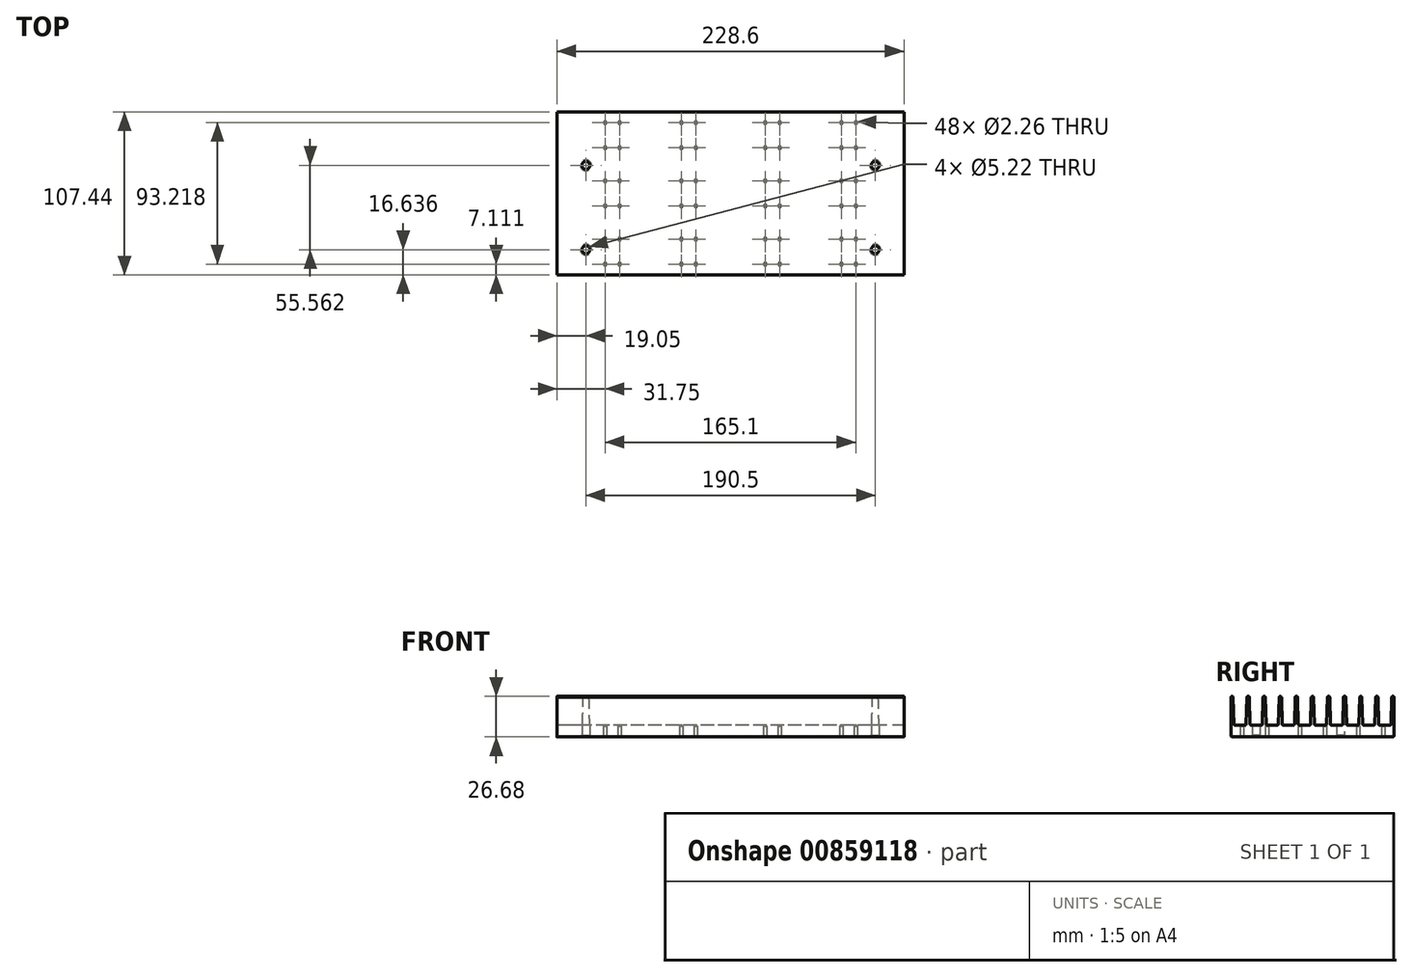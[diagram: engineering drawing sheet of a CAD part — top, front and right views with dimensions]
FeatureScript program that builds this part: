
annotation { "Feature Type Name" : "Feature", "Feature Type Description" : "" }
export const myFeature = defineFeature(function(context is Context, id is Id, definition is map)
    precondition{}
    {
        {
            var Q0;
            Q0=qCreatedBy(makeId("Right.planeOp"),FACE);
            var sketch = newSketch(context, id + "F0", { "sketchPlane" : qUnion([Q0])});
            skLineSegment(sketch, "E0", {"start": v(50.94, -5.71) * mm, "end": v(44.38, -5.71) * mm});
            skArc(sketch, "E1", {"start": v(43.62, -4.97) * mm, "mid": v(43.85, -5.5) * mm, "end": v(44.38, -5.71) * mm});
            skLineSegment(sketch, "E2", {"start": v(43.62, -4.97) * mm, "end": v(43.13, 12.59) * mm});
            skArc(sketch, "E3", {"start": v(43.13, 12.59) * mm, "mid": v(42.37, 13.33) * mm, "end": v(41.6, 12.59) * mm});
            skLineSegment(sketch, "E4", {"start": v(41.6, 12.59) * mm, "end": v(41.11, -4.97) * mm});
            skArc(sketch, "E5", {"start": v(40.35, -5.71) * mm, "mid": v(40.88, -5.5) * mm, "end": v(41.11, -4.97) * mm});
            skLineSegment(sketch, "E6", {"start": v(40.35, -5.71) * mm, "end": v(33.8, -5.71) * mm});
            skArc(sketch, "E7", {"start": v(33.03, -4.97) * mm, "mid": v(33.26, -5.5) * mm, "end": v(33.8, -5.71) * mm});
            skLineSegment(sketch, "E8", {"start": v(33.03, -4.97) * mm, "end": v(32.54, 12.59) * mm});
            skArc(sketch, "E9", {"start": v(32.54, 12.59) * mm, "mid": v(31.78, 13.33) * mm, "end": v(31.01, 12.59) * mm});
            skLineSegment(sketch, "E10", {"start": v(31.01, 12.59) * mm, "end": v(30.52, -4.97) * mm});
            skArc(sketch, "E11", {"start": v(29.76, -5.71) * mm, "mid": v(30.3, -5.5) * mm, "end": v(30.52, -4.97) * mm});
            skLineSegment(sketch, "E12", {"start": v(29.76, -5.71) * mm, "end": v(23.2, -5.71) * mm});
            skArc(sketch, "E13", {"start": v(22.44, -4.97) * mm, "mid": v(22.67, -5.5) * mm, "end": v(23.2, -5.71) * mm});
            skLineSegment(sketch, "E14", {"start": v(22.44, -4.97) * mm, "end": v(21.95, 12.59) * mm});
            skArc(sketch, "E15", {"start": v(21.95, 12.59) * mm, "mid": v(21.18, 13.33) * mm, "end": v(20.42, 12.59) * mm});
            skLineSegment(sketch, "E16", {"start": v(20.42, 12.59) * mm, "end": v(19.93, -4.97) * mm});
            skArc(sketch, "E17", {"start": v(19.17, -5.71) * mm, "mid": v(19.7, -5.5) * mm, "end": v(19.93, -4.97) * mm});
            skLineSegment(sketch, "E18", {"start": v(19.17, -5.71) * mm, "end": v(12.6, -5.71) * mm});
            skArc(sketch, "E19", {"start": v(11.85, -4.97) * mm, "mid": v(12.08, -5.5) * mm, "end": v(12.6, -5.71) * mm});
            skLineSegment(sketch, "E20", {"start": v(11.85, -4.97) * mm, "end": v(11.35, 12.59) * mm});
            skArc(sketch, "E21", {"start": v(11.35, 12.59) * mm, "mid": v(10.6, 13.33) * mm, "end": v(9.83, 12.59) * mm});
            skLineSegment(sketch, "E22", {"start": v(9.83, 12.59) * mm, "end": v(9.34, -4.97) * mm});
            skArc(sketch, "E23", {"start": v(8.58, -5.71) * mm, "mid": v(9.1, -5.5) * mm, "end": v(9.34, -4.97) * mm});
            skLineSegment(sketch, "E24", {"start": v(8.58, -5.71) * mm, "end": v(2.02, -5.71) * mm});
            skArc(sketch, "E25", {"start": v(1.25, -4.97) * mm, "mid": v(1.48, -5.5) * mm, "end": v(2.02, -5.71) * mm});
            skLineSegment(sketch, "E26", {"start": v(1.25, -4.97) * mm, "end": v(0.76, 12.59) * mm});
            skArc(sketch, "E27", {"start": v(0.76, 12.59) * mm, "mid": v(0, 13.33) * mm, "end": v(-0.76, 12.59) * mm});
            skLineSegment(sketch, "E28", {"start": v(-0.76, 12.59) * mm, "end": v(-1.25, -4.97) * mm});
            skArc(sketch, "E29", {"start": v(-2.02, -5.71) * mm, "mid": v(-1.48, -5.5) * mm, "end": v(-1.25, -4.97) * mm});
            skLineSegment(sketch, "E30", {"start": v(-2.02, -5.71) * mm, "end": v(-8.58, -5.71) * mm});
            skArc(sketch, "E31", {"start": v(-9.34, -4.97) * mm, "mid": v(-9.1, -5.5) * mm, "end": v(-8.58, -5.71) * mm});
            skLineSegment(sketch, "E32", {"start": v(-9.34, -4.97) * mm, "end": v(-9.83, 12.59) * mm});
            skArc(sketch, "E33", {"start": v(-9.83, 12.59) * mm, "mid": v(-10.6, 13.33) * mm, "end": v(-11.35, 12.59) * mm});
            skLineSegment(sketch, "E34", {"start": v(-11.35, 12.59) * mm, "end": v(-11.85, -4.97) * mm});
            skArc(sketch, "E35", {"start": v(-12.6, -5.71) * mm, "mid": v(-12.08, -5.5) * mm, "end": v(-11.85, -4.97) * mm});
            skLineSegment(sketch, "E36", {"start": v(-12.6, -5.71) * mm, "end": v(-19.17, -5.71) * mm});
            skArc(sketch, "E37", {"start": v(-19.93, -4.97) * mm, "mid": v(-19.7, -5.5) * mm, "end": v(-19.17, -5.71) * mm});
            skLineSegment(sketch, "E38", {"start": v(-19.93, -4.97) * mm, "end": v(-20.42, 12.59) * mm});
            skArc(sketch, "E39", {"start": v(-20.42, 12.59) * mm, "mid": v(-21.18, 13.34) * mm, "end": v(-21.95, 12.59) * mm});
            skLineSegment(sketch, "E40", {"start": v(-21.95, 12.59) * mm, "end": v(-22.44, -4.97) * mm});
            skArc(sketch, "E41", {"start": v(-23.2, -5.71) * mm, "mid": v(-22.67, -5.5) * mm, "end": v(-22.44, -4.97) * mm});
            skLineSegment(sketch, "E42", {"start": v(-23.2, -5.71) * mm, "end": v(-29.76, -5.71) * mm});
            skArc(sketch, "E43", {"start": v(-30.52, -4.97) * mm, "mid": v(-30.3, -5.5) * mm, "end": v(-29.76, -5.71) * mm});
            skLineSegment(sketch, "E44", {"start": v(-30.52, -4.97) * mm, "end": v(-31.01, 12.59) * mm});
            skArc(sketch, "E45", {"start": v(-31.01, 12.59) * mm, "mid": v(-31.78, 13.33) * mm, "end": v(-32.54, 12.59) * mm});
            skLineSegment(sketch, "E46", {"start": v(-32.54, 12.59) * mm, "end": v(-33.03, -4.97) * mm});
            skArc(sketch, "E47", {"start": v(-33.8, -5.71) * mm, "mid": v(-33.26, -5.5) * mm, "end": v(-33.03, -4.97) * mm});
            skLineSegment(sketch, "E48", {"start": v(-33.8, -5.71) * mm, "end": v(-40.35, -5.71) * mm});
            skArc(sketch, "E49", {"start": v(-41.11, -4.97) * mm, "mid": v(-40.88, -5.5) * mm, "end": v(-40.35, -5.71) * mm});
            skLineSegment(sketch, "E50", {"start": v(-41.11, -4.97) * mm, "end": v(-41.6, 12.59) * mm});
            skArc(sketch, "E51", {"start": v(-41.6, 12.59) * mm, "mid": v(-42.37, 13.33) * mm, "end": v(-43.13, 12.59) * mm});
            skLineSegment(sketch, "E52", {"start": v(-43.13, 12.59) * mm, "end": v(-43.62, -4.97) * mm});
            skArc(sketch, "E53", {"start": v(-44.38, -5.71) * mm, "mid": v(-43.85, -5.5) * mm, "end": v(-43.62, -4.97) * mm});
            skLineSegment(sketch, "E54", {"start": v(-44.38, -5.71) * mm, "end": v(-50.94, -5.71) * mm});
            skArc(sketch, "E55", {"start": v(-51.7, -4.97) * mm, "mid": v(-51.48, -5.5) * mm, "end": v(-50.94, -5.71) * mm});
            skLineSegment(sketch, "E56", {"start": v(-51.7, -4.97) * mm, "end": v(-52.2, 12.59) * mm});
            skArc(sketch, "E57", {"start": v(-52.2, 12.59) * mm, "mid": v(-52.96, 13.34) * mm, "end": v(-53.72, 12.59) * mm});
            skLineSegment(sketch, "E58", {"start": v(-53.72, 12.59) * mm, "end": v(-53.72, -12.57) * mm});
            skArc(sketch, "E59", {"start": v(-53.72, -12.57) * mm, "mid": v(-53.5, -13.11) * mm, "end": v(-52.96, -13.34) * mm});
            skLineSegment(sketch, "E60", {"start": v(-52.96, -13.33) * mm, "end": v(52.96, -13.33) * mm});
            skArc(sketch, "E61", {"start": v(52.96, -13.34) * mm, "mid": v(53.5, -13.11) * mm, "end": v(53.72, -12.57) * mm});
            skLineSegment(sketch, "E62", {"start": v(53.72, -12.57) * mm, "end": v(53.72, 12.59) * mm});
            skArc(sketch, "E63", {"start": v(53.72, 12.59) * mm, "mid": v(52.96, 13.33) * mm, "end": v(52.2, 12.59) * mm});
            skLineSegment(sketch, "E64", {"start": v(52.2, 12.59) * mm, "end": v(51.7, -4.97) * mm});
            skArc(sketch, "E65", {"start": v(50.94, -5.71) * mm, "mid": v(51.48, -5.5) * mm, "end": v(51.7, -4.97) * mm});
            skSolve(sketch);
        }
        {
            var Q0;
            Q0=qSketchRegion(id+"F0",true);
            extrude(context, id + "F1", {"entities" : qUnion([Q0]), "endBound" : BoundingType.SYMMETRIC, "depth" : 228.6 * mm, "offsetDistance" : 25.4 * mm});
        }
        {
            var Q0;
            Q0=makeQuery(id+"F1.opExtrude","SWEPT_FACE",FACE,{"disambiguationData":[OSD([sQuery(id+"F0.wireOp",EDGE,"E60")])]});
            var sketch = newSketch(context, id + "F2", { "sketchPlane" : qUnion([Q0])});
            skLineSegment(sketch, "E66.0", {"start": v(-114.3, 52.96) * mm, "end": v(-114.3, -52.96) * mm});
            skLineSegment(sketch, "E67.0.2", {"start": v(114.3, -52.96) * mm, "end": v(114.3, 52.96) * mm});
            skPoint(sketch, "E68", {"position": v(-95.25, 37.08) * mm});
            skPoint(sketch, "E69", {"position": v(95.25, 37.08) * mm});
            skPoint(sketch, "E70", {"position": v(14.56, 92.82) * mm});
            skPoint(sketch, "E71", {"position": v(-95.25, -18.48) * mm});
            skPoint(sketch, "E72", {"position": v(95.25, -18.48) * mm});
            skSolve(sketch);
        }
        {
            var Q0;
            Q0=sQuery(id+"F2.wireOp",VERTEX,"E68");
            var Q1;
            Q1=sQuery(id+"F2.wireOp",VERTEX,"E71");
            var Q2;
            Q2=sQuery(id+"F2.wireOp",VERTEX,"E69");
            var Q3;
            Q3=sQuery(id+"F2.wireOp",VERTEX,"E72");
            var Q4;
            Q4=makeQuery(id+"F1.opExtrude","SWEPT_BODY",BODY,{"disambiguationData":[OSD([sQuery(id+"F0.wireOp",EDGE,"E0"),sQuery(id+"F0.wireOp",EDGE,"E1"),sQuery(id+"F0.wireOp",EDGE,"E2"),sQuery(id+"F0.wireOp",EDGE,"E3"),sQuery(id+"F0.wireOp",EDGE,"E4"),sQuery(id+"F0.wireOp",EDGE,"E5"),sQuery(id+"F0.wireOp",EDGE,"E6"),sQuery(id+"F0.wireOp",EDGE,"E7"),sQuery(id+"F0.wireOp",EDGE,"E8"),sQuery(id+"F0.wireOp",EDGE,"E9"),sQuery(id+"F0.wireOp",EDGE,"E10"),sQuery(id+"F0.wireOp",EDGE,"E11"),sQuery(id+"F0.wireOp",EDGE,"E12"),sQuery(id+"F0.wireOp",EDGE,"E13"),sQuery(id+"F0.wireOp",EDGE,"E14"),sQuery(id+"F0.wireOp",EDGE,"E15"),sQuery(id+"F0.wireOp",EDGE,"E16"),sQuery(id+"F0.wireOp",EDGE,"E17"),sQuery(id+"F0.wireOp",EDGE,"E18"),sQuery(id+"F0.wireOp",EDGE,"E19"),sQuery(id+"F0.wireOp",EDGE,"E20"),sQuery(id+"F0.wireOp",EDGE,"E21"),sQuery(id+"F0.wireOp",EDGE,"E22"),sQuery(id+"F0.wireOp",EDGE,"E23"),sQuery(id+"F0.wireOp",EDGE,"E24"),sQuery(id+"F0.wireOp",EDGE,"E25"),sQuery(id+"F0.wireOp",EDGE,"E26"),sQuery(id+"F0.wireOp",EDGE,"E27"),sQuery(id+"F0.wireOp",EDGE,"E28"),sQuery(id+"F0.wireOp",EDGE,"E29"),sQuery(id+"F0.wireOp",EDGE,"E30"),sQuery(id+"F0.wireOp",EDGE,"E31"),sQuery(id+"F0.wireOp",EDGE,"E32"),sQuery(id+"F0.wireOp",EDGE,"E33"),sQuery(id+"F0.wireOp",EDGE,"E34"),sQuery(id+"F0.wireOp",EDGE,"E35"),sQuery(id+"F0.wireOp",EDGE,"E36"),sQuery(id+"F0.wireOp",EDGE,"E37"),sQuery(id+"F0.wireOp",EDGE,"E38"),sQuery(id+"F0.wireOp",EDGE,"E39"),sQuery(id+"F0.wireOp",EDGE,"E40"),sQuery(id+"F0.wireOp",EDGE,"E41"),sQuery(id+"F0.wireOp",EDGE,"E42"),sQuery(id+"F0.wireOp",EDGE,"E43"),sQuery(id+"F0.wireOp",EDGE,"E44"),sQuery(id+"F0.wireOp",EDGE,"E45"),sQuery(id+"F0.wireOp",EDGE,"E46"),sQuery(id+"F0.wireOp",EDGE,"E47"),sQuery(id+"F0.wireOp",EDGE,"E48"),sQuery(id+"F0.wireOp",EDGE,"E49"),sQuery(id+"F0.wireOp",EDGE,"E50"),sQuery(id+"F0.wireOp",EDGE,"E51"),sQuery(id+"F0.wireOp",EDGE,"E52"),sQuery(id+"F0.wireOp",EDGE,"E53"),sQuery(id+"F0.wireOp",EDGE,"E54"),sQuery(id+"F0.wireOp",EDGE,"E55"),sQuery(id+"F0.wireOp",EDGE,"E56"),sQuery(id+"F0.wireOp",EDGE,"E57"),sQuery(id+"F0.wireOp",EDGE,"E58"),sQuery(id+"F0.wireOp",EDGE,"E59"),sQuery(id+"F0.wireOp",EDGE,"E60"),sQuery(id+"F0.wireOp",EDGE,"E61"),sQuery(id+"F0.wireOp",EDGE,"E62"),sQuery(id+"F0.wireOp",EDGE,"E63"),sQuery(id+"F0.wireOp",EDGE,"E64"),sQuery(id+"F0.wireOp",EDGE,"E65")])]});
            hole(context, id + "F3", {"style" : HoleStyle.C_SINK, "endStyle" : HoleEndStyle.THROUGH, "standardTappedOrClearance" : lookupTablePath({ "standard" : "ANSI", "size" : "#5 (0.2)", "type" : "Drilled" }), "standardBlindInLast" : lookupTablePath({ "standard" : "ANSI", "size" : "#5", "type" : "Drilled" }), "holeDiameter" : 5.22 * mm, "cSinkDiameter" : 7.14 * mm, "cSinkAngle" : 82 * degree, "majorDiameter" : 2.84 * mm, "isTappedThrough" : true, "tappedDepth" : 5.2 * mm, "tapClearance" : 3, "locations" : qUnion([Q0, Q1, Q2, Q3]), "scope" : qUnion([Q4])});
        }
        {
            var Q0;
            Q0=makeQuery(id+"F1.opExtrude","SWEPT_FACE",FACE,{"disambiguationData":[OSD([sQuery(id+"F0.wireOp",EDGE,"E60")])]});
            var sketch = newSketch(context, id + "F4", { "sketchPlane" : qUnion([Q0])});
            skPoint(sketch, "E73", {"position": v(-82.55, 46.6) * mm});
            skPoint(sketch, "E74", {"position": v(-73.03, 46.6) * mm});
            skPoint(sketch, "E75", {"position": v(-82.55, 30.1) * mm});
            skPoint(sketch, "E76", {"position": v(-73.03, 30.1) * mm});
            skPoint(sketch, "E77", {"position": v(-32.38, 46.6) * mm});
            skPoint(sketch, "E78", {"position": v(-22.86, 46.6) * mm});
            skPoint(sketch, "E79", {"position": v(-32.38, 30.1) * mm});
            skPoint(sketch, "E80", {"position": v(-22.86, 30.1) * mm});
            skPoint(sketch, "E81.MirrorP", {"position": v(82.55, 46.6) * mm});
            skPoint(sketch, "E82.MirrorP", {"position": v(73.03, 46.6) * mm});
            skPoint(sketch, "E83.MirrorP", {"position": v(82.55, 30.1) * mm});
            skPoint(sketch, "E84.MirrorP", {"position": v(73.03, 30.1) * mm});
            skPoint(sketch, "E85.MirrorP", {"position": v(32.38, 46.6) * mm});
            skPoint(sketch, "E86.MirrorP", {"position": v(22.86, 46.6) * mm});
            skPoint(sketch, "E87.MirrorP", {"position": v(22.86, 30.1) * mm});
            skPoint(sketch, "E88.MirrorP", {"position": v(32.38, 30.1) * mm});
            skPoint(sketch, "E89.MirrorP", {"position": v(-82.55, -46.6) * mm});
            skPoint(sketch, "E90.MirrorP", {"position": v(-73.03, -46.6) * mm});
            skPoint(sketch, "E91.MirrorP", {"position": v(-73.03, -30.1) * mm});
            skPoint(sketch, "E92.MirrorP", {"position": v(-82.55, -30.1) * mm});
            skPoint(sketch, "E93.MirrorP", {"position": v(-32.38, -46.6) * mm});
            skPoint(sketch, "E94.MirrorP", {"position": v(-22.86, -46.6) * mm});
            skPoint(sketch, "E95.MirrorP", {"position": v(-22.86, -30.1) * mm});
            skPoint(sketch, "E96.MirrorP", {"position": v(-32.38, -30.1) * mm});
            skPoint(sketch, "E97.MirrorP", {"position": v(22.86, -46.6) * mm});
            skPoint(sketch, "E98.MirrorP", {"position": v(32.38, -46.6) * mm});
            skPoint(sketch, "E99.MirrorP", {"position": v(22.86, -30.1) * mm});
            skPoint(sketch, "E100.MirrorP", {"position": v(32.38, -30.1) * mm});
            skPoint(sketch, "E101.MirrorP", {"position": v(73.03, -46.6) * mm});
            skPoint(sketch, "E102.MirrorP", {"position": v(82.55, -46.6) * mm});
            skPoint(sketch, "E103.MirrorP", {"position": v(82.55, -30.1) * mm});
            skPoint(sketch, "E104.MirrorP", {"position": v(73.03, -30.1) * mm});
            skPoint(sketch, "E105", {"position": v(-82.55, 8.25) * mm});
            skPoint(sketch, "E106", {"position": v(-82.55, -8.26) * mm});
            skPoint(sketch, "E107", {"position": v(-73.02, 8.25) * mm});
            skPoint(sketch, "E108", {"position": v(-73.02, -8.26) * mm});
            skPoint(sketch, "E109", {"position": v(-32.38, 8.25) * mm});
            skPoint(sketch, "E110", {"position": v(-22.86, 8.25) * mm});
            skPoint(sketch, "E111", {"position": v(-32.38, -8.26) * mm});
            skPoint(sketch, "E112", {"position": v(-22.86, -8.26) * mm});
            skPoint(sketch, "E113.MirrorP", {"position": v(82.55, 8.25) * mm});
            skPoint(sketch, "E114.MirrorP", {"position": v(73.02, 8.25) * mm});
            skPoint(sketch, "E115.MirrorP", {"position": v(32.38, 8.25) * mm});
            skPoint(sketch, "E116.MirrorP", {"position": v(22.86, 8.25) * mm});
            skPoint(sketch, "E117.MirrorP", {"position": v(22.86, -8.26) * mm});
            skPoint(sketch, "E118.MirrorP", {"position": v(32.38, -8.26) * mm});
            skPoint(sketch, "E119.MirrorP", {"position": v(73.02, -8.26) * mm});
            skPoint(sketch, "E120.MirrorP", {"position": v(82.55, -8.26) * mm});
            skSolve(sketch);
        }
        {
            var Q0;
            Q0=sQuery(id+"F4.wireOp",VERTEX,"E73");
            var Q1;
            Q1=sQuery(id+"F4.wireOp",VERTEX,"E74");
            var Q2;
            Q2=sQuery(id+"F4.wireOp",VERTEX,"E76");
            var Q3;
            Q3=sQuery(id+"F4.wireOp",VERTEX,"E75");
            var Q4;
            Q4=sQuery(id+"F4.wireOp",VERTEX,"E105");
            var Q5;
            Q5=sQuery(id+"F4.wireOp",VERTEX,"E107");
            var Q6;
            Q6=sQuery(id+"F4.wireOp",VERTEX,"E108");
            var Q7;
            Q7=sQuery(id+"F4.wireOp",VERTEX,"E106");
            var Q8;
            Q8=sQuery(id+"F4.wireOp",VERTEX,"E92.MirrorP");
            var Q9;
            Q9=sQuery(id+"F4.wireOp",VERTEX,"E91.MirrorP");
            var Q10;
            Q10=sQuery(id+"F4.wireOp",VERTEX,"E90.MirrorP");
            var Q11;
            Q11=sQuery(id+"F4.wireOp",VERTEX,"E89.MirrorP");
            var Q12;
            Q12=sQuery(id+"F4.wireOp",VERTEX,"E77");
            var Q13;
            Q13=sQuery(id+"F4.wireOp",VERTEX,"E78");
            var Q14;
            Q14=sQuery(id+"F4.wireOp",VERTEX,"E80");
            var Q15;
            Q15=sQuery(id+"F4.wireOp",VERTEX,"E79");
            var Q16;
            Q16=sQuery(id+"F4.wireOp",VERTEX,"E109");
            var Q17;
            Q17=sQuery(id+"F4.wireOp",VERTEX,"E110");
            var Q18;
            Q18=sQuery(id+"F4.wireOp",VERTEX,"E112");
            var Q19;
            Q19=sQuery(id+"F4.wireOp",VERTEX,"E111");
            var Q20;
            Q20=sQuery(id+"F4.wireOp",VERTEX,"E96.MirrorP");
            var Q21;
            Q21=sQuery(id+"F4.wireOp",VERTEX,"E95.MirrorP");
            var Q22;
            Q22=sQuery(id+"F4.wireOp",VERTEX,"E94.MirrorP");
            var Q23;
            Q23=sQuery(id+"F4.wireOp",VERTEX,"E93.MirrorP");
            var Q24;
            Q24=sQuery(id+"F4.wireOp",VERTEX,"E86.MirrorP");
            var Q25;
            Q25=sQuery(id+"F4.wireOp",VERTEX,"E85.MirrorP");
            var Q26;
            Q26=sQuery(id+"F4.wireOp",VERTEX,"E87.MirrorP");
            var Q27;
            Q27=sQuery(id+"F4.wireOp",VERTEX,"E88.MirrorP");
            var Q28;
            Q28=sQuery(id+"F4.wireOp",VERTEX,"E116.MirrorP");
            var Q29;
            Q29=sQuery(id+"F4.wireOp",VERTEX,"E115.MirrorP");
            var Q30;
            Q30=sQuery(id+"F4.wireOp",VERTEX,"E117.MirrorP");
            var Q31;
            Q31=sQuery(id+"F4.wireOp",VERTEX,"E118.MirrorP");
            var Q32;
            Q32=sQuery(id+"F4.wireOp",VERTEX,"E99.MirrorP");
            var Q33;
            Q33=sQuery(id+"F4.wireOp",VERTEX,"E100.MirrorP");
            var Q34;
            Q34=sQuery(id+"F4.wireOp",VERTEX,"E97.MirrorP");
            var Q35;
            Q35=sQuery(id+"F4.wireOp",VERTEX,"E98.MirrorP");
            var Q36;
            Q36=sQuery(id+"F4.wireOp",VERTEX,"E82.MirrorP");
            var Q37;
            Q37=sQuery(id+"F4.wireOp",VERTEX,"E81.MirrorP");
            var Q38;
            Q38=sQuery(id+"F4.wireOp",VERTEX,"E84.MirrorP");
            var Q39;
            Q39=sQuery(id+"F4.wireOp",VERTEX,"E83.MirrorP");
            var Q40;
            Q40=sQuery(id+"F4.wireOp",VERTEX,"E114.MirrorP");
            var Q41;
            Q41=sQuery(id+"F4.wireOp",VERTEX,"E113.MirrorP");
            var Q42;
            Q42=sQuery(id+"F4.wireOp",VERTEX,"E119.MirrorP");
            var Q43;
            Q43=sQuery(id+"F4.wireOp",VERTEX,"E120.MirrorP");
            var Q44;
            Q44=sQuery(id+"F4.wireOp",VERTEX,"E104.MirrorP");
            var Q45;
            Q45=sQuery(id+"F4.wireOp",VERTEX,"E103.MirrorP");
            var Q46;
            Q46=sQuery(id+"F4.wireOp",VERTEX,"E102.MirrorP");
            var Q47;
            Q47=sQuery(id+"F4.wireOp",VERTEX,"E101.MirrorP");
            var Q48;
            Q48=makeQuery(id+"F1.opExtrude","SWEPT_BODY",BODY,{"disambiguationData":[OSD([sQuery(id+"F0.wireOp",EDGE,"E0"),sQuery(id+"F0.wireOp",EDGE,"E1"),sQuery(id+"F0.wireOp",EDGE,"E2"),sQuery(id+"F0.wireOp",EDGE,"E3"),sQuery(id+"F0.wireOp",EDGE,"E4"),sQuery(id+"F0.wireOp",EDGE,"E5"),sQuery(id+"F0.wireOp",EDGE,"E6"),sQuery(id+"F0.wireOp",EDGE,"E7"),sQuery(id+"F0.wireOp",EDGE,"E8"),sQuery(id+"F0.wireOp",EDGE,"E9"),sQuery(id+"F0.wireOp",EDGE,"E10"),sQuery(id+"F0.wireOp",EDGE,"E11"),sQuery(id+"F0.wireOp",EDGE,"E12"),sQuery(id+"F0.wireOp",EDGE,"E13"),sQuery(id+"F0.wireOp",EDGE,"E14"),sQuery(id+"F0.wireOp",EDGE,"E15"),sQuery(id+"F0.wireOp",EDGE,"E16"),sQuery(id+"F0.wireOp",EDGE,"E17"),sQuery(id+"F0.wireOp",EDGE,"E18"),sQuery(id+"F0.wireOp",EDGE,"E19"),sQuery(id+"F0.wireOp",EDGE,"E20"),sQuery(id+"F0.wireOp",EDGE,"E21"),sQuery(id+"F0.wireOp",EDGE,"E22"),sQuery(id+"F0.wireOp",EDGE,"E23"),sQuery(id+"F0.wireOp",EDGE,"E24"),sQuery(id+"F0.wireOp",EDGE,"E25"),sQuery(id+"F0.wireOp",EDGE,"E26"),sQuery(id+"F0.wireOp",EDGE,"E27"),sQuery(id+"F0.wireOp",EDGE,"E28"),sQuery(id+"F0.wireOp",EDGE,"E29"),sQuery(id+"F0.wireOp",EDGE,"E30"),sQuery(id+"F0.wireOp",EDGE,"E31"),sQuery(id+"F0.wireOp",EDGE,"E32"),sQuery(id+"F0.wireOp",EDGE,"E33"),sQuery(id+"F0.wireOp",EDGE,"E34"),sQuery(id+"F0.wireOp",EDGE,"E35"),sQuery(id+"F0.wireOp",EDGE,"E36"),sQuery(id+"F0.wireOp",EDGE,"E37"),sQuery(id+"F0.wireOp",EDGE,"E38"),sQuery(id+"F0.wireOp",EDGE,"E39"),sQuery(id+"F0.wireOp",EDGE,"E40"),sQuery(id+"F0.wireOp",EDGE,"E41"),sQuery(id+"F0.wireOp",EDGE,"E42"),sQuery(id+"F0.wireOp",EDGE,"E43"),sQuery(id+"F0.wireOp",EDGE,"E44"),sQuery(id+"F0.wireOp",EDGE,"E45"),sQuery(id+"F0.wireOp",EDGE,"E46"),sQuery(id+"F0.wireOp",EDGE,"E47"),sQuery(id+"F0.wireOp",EDGE,"E48"),sQuery(id+"F0.wireOp",EDGE,"E49"),sQuery(id+"F0.wireOp",EDGE,"E50"),sQuery(id+"F0.wireOp",EDGE,"E51"),sQuery(id+"F0.wireOp",EDGE,"E52"),sQuery(id+"F0.wireOp",EDGE,"E53"),sQuery(id+"F0.wireOp",EDGE,"E54"),sQuery(id+"F0.wireOp",EDGE,"E55"),sQuery(id+"F0.wireOp",EDGE,"E56"),sQuery(id+"F0.wireOp",EDGE,"E57"),sQuery(id+"F0.wireOp",EDGE,"E58"),sQuery(id+"F0.wireOp",EDGE,"E59"),sQuery(id+"F0.wireOp",EDGE,"E60"),sQuery(id+"F0.wireOp",EDGE,"E61"),sQuery(id+"F0.wireOp",EDGE,"E62"),sQuery(id+"F0.wireOp",EDGE,"E63"),sQuery(id+"F0.wireOp",EDGE,"E64"),sQuery(id+"F0.wireOp",EDGE,"E65")])]});
            hole(context, id + "F5", {"style" : HoleStyle.SIMPLE, "endStyle" : HoleEndStyle.BLIND, "standardTappedOrClearance" : lookupTablePath({ "standard" : "ANSI", "engagement" : "75%", "pitch" : "40 tpi", "size" : "#4", "type" : "Tapped" }), "standardBlindInLast" : lookupTablePath({ "standard" : "ANSI", "engagement" : "75%", "pitch" : "40 tpi", "size" : "#4", "type" : "Tapped" }), "holeDiameter" : 2.26 * mm, "majorDiameter" : 2.84 * mm, "showTappedDepth" : true, "holeDepth" : 7.11 * mm, "isTappedThrough" : true, "tappedDepth" : 5.2 * mm, "tapClearance" : 3, "locations" : qUnion([Q0, Q1, Q2, Q3, Q4, Q5, Q6, Q7, Q8, Q9, Q10, Q11, Q12, Q13, Q14, Q15, Q16, Q17, Q18, Q19, Q20, Q21, Q22, Q23, Q24, Q25, Q26, Q27, Q28, Q29, Q30, Q31, Q32, Q33, Q34, Q35, Q36, Q37, Q38, Q39, Q40, Q41, Q42, Q43, Q44, Q45, Q46, Q47]), "scope" : qUnion([Q48])});
        }
    });
